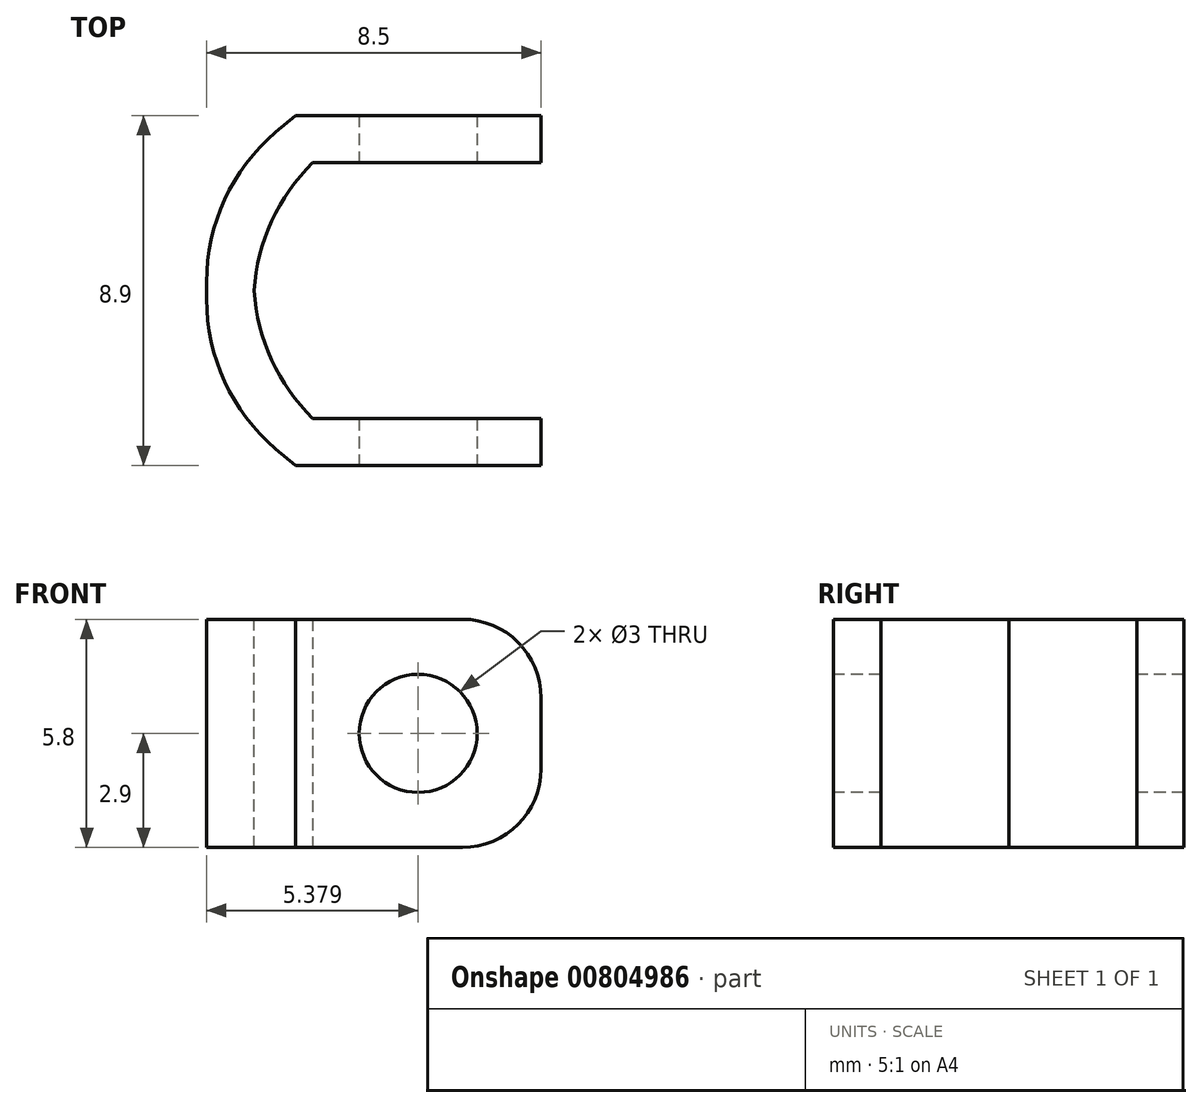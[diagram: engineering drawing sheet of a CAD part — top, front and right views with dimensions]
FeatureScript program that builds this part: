
annotation { "Feature Type Name" : "Feature", "Feature Type Description" : "" }
export const myFeature = defineFeature(function(context is Context, id is Id, definition is map)
    precondition{}
    {
        {
            assignVariable(context, id + "F0", {"name" : "nutWidth", "anyValue" : 5.8 * mm});
        }
        {
            var Q0;
            Q0=qCreatedBy(makeId("Top.planeOp"),FACE);
            var sketch = newSketch(context, id + "F1", { "sketchPlane" : qUnion([Q0])});
            skLineSegment(sketch, "E0", {"start": v(-7.3, 0) * mm, "end": v(-7.3, 1.97) * mm});
            skLineSegment(sketch, "E1", {"start": v(-7.3, 1.97) * mm, "end": v(-5.8, 3.25) * mm});
            skLineSegment(sketch, "E2", {"start": v(-5.8, 3.25) * mm, "end": v(0, 3.25) * mm});
            skLineSegment(sketch, "E3.MirrorCS", {"start": v(-7.3, 0) * mm, "end": v(-7.3, -1.97) * mm});
            skLineSegment(sketch, "E4.MirrorCS", {"start": v(-7.3, -1.97) * mm, "end": v(-5.8, -3.25) * mm});
            skLineSegment(sketch, "E5.MirrorCS", {"start": v(-5.8, -3.25) * mm, "end": v(0, -3.25) * mm});
            skLineSegment(sketch, "E6.0", {"start": v(-6.24, 4.45) * mm, "end": v(0, 4.45) * mm});
            skLineSegment(sketch, "E6.1", {"start": v(-8.5, 2.52) * mm, "end": v(-6.24, 4.45) * mm});
            skLineSegment(sketch, "E6.2", {"start": v(-6.24, -4.45) * mm, "end": v(0, -4.45) * mm});
            skLineSegment(sketch, "E6.3", {"start": v(-8.5, -2.52) * mm, "end": v(-6.24, -4.45) * mm});
            skLineSegment(sketch, "E6.4", {"start": v(-8.5, 0) * mm, "end": v(-8.5, -2.52) * mm});
            skLineSegment(sketch, "E6.5", {"start": v(-8.5, 0) * mm, "end": v(-8.5, 2.52) * mm});
            skLineSegment(sketch, "E7", {"start": v(0, 4.45) * mm, "end": v(0, 3.25) * mm});
            skLineSegment(sketch, "E8", {"start": v(0, -3.25) * mm, "end": v(0, -4.45) * mm});
            skSolve(sketch);
        }
        {
            var Q0;
            Q0 = qSketchRegion(id + "F1", true);
            extrude(context, id + "F2", {"entities" : qUnion([Q0]), "depth" : getVariable(context, 'nutWidth'), "offsetDistance" : 25 * mm});
        }
        {
            var Q0;
            Q0=makeQuery(id+"F2.opExtrude","SWEPT_EDGE",EDGE,{"disambiguationData":[OSD([sQuery(id+"F1.wireOp",EDGE,"E6.3"),sQuery(id+"F1.wireOp",EDGE,"E6.4")])]});
            var Q1;
            Q1=makeQuery(id+"F2.opExtrude","SWEPT_EDGE",EDGE,{"disambiguationData":[OSD([sQuery(id+"F1.wireOp",EDGE,"E6.1"),sQuery(id+"F1.wireOp",EDGE,"E6.5")])]});
            var Q2;
            Q2=makeQuery(id+"F2.opExtrude","SWEPT_EDGE",EDGE,{"disambiguationData":[OSD([sQuery(id+"F1.wireOp",EDGE,"E3.MirrorCS"),sQuery(id+"F1.wireOp",EDGE,"E4.MirrorCS")])]});
            var Q3;
            Q3=makeQuery(id+"F2.opExtrude","SWEPT_EDGE",EDGE,{"disambiguationData":[OSD([sQuery(id+"F1.wireOp",EDGE,"E0"),sQuery(id+"F1.wireOp",EDGE,"E1")])]});
            fillet(context, id + "F3", {"entities" : qUnion([Q0, Q1, Q2, Q3]), "radius" : 5 * mm, "tangentPropagation" : true, "allowEdgeOverflow" : false});
        }
        {
            var Q0;
            Q0=makeQuery(id+"F2.opExtrude","SWEPT_FACE",FACE,{"disambiguationData":[OSD([sQuery(id+"F1.wireOp",EDGE,"E6.2")])]});
            var sketch = newSketch(context, id + "F4", { "sketchPlane" : qUnion([Q0])});
            skLineSegment(sketch, "E9", {"start": v(-6.24, 2.9) * mm, "end": v(0, 2.9) * mm});
            skLineSegment(sketch, "E10", {"start": v(0, 2.9) * mm, "end": v(-3.12, 2.9) * mm});
            skCircle(sketch, "E11", {"center": v(-3.12, 2.9) * mm, "radius": 1.5 * mm});
            skSolve(sketch);
        }
        {
            var Q0;
            Q0 = qSketchRegion(id + "F4", true);
            extrude(context, id + "F5", {"entities" : qUnion([Q0]), "operationType" : NewBodyOperationType.REMOVE, "endBound" : BoundingType.THROUGH_ALL, "oppositeDirection" : true, "depth" : 25 * mm, "offsetDistance" : 25 * mm});
        }
        {
            var Q0;
            Q0=makeQuery(id+"F2.opExtrude","CAP_EDGE",EDGE,{"disambiguationData":[OSD([sQuery(id+"F1.wireOp",EDGE,"E7")])],"isStart":false});
            var Q1;
            Q1=makeQuery(id+"F2.opExtrude","CAP_EDGE",EDGE,{"disambiguationData":[OSD([sQuery(id+"F1.wireOp",EDGE,"E8")])],"isStart":false});
            var Q2;
            Q2=makeQuery(id+"F2.opExtrude","CAP_EDGE",EDGE,{"disambiguationData":[OSD([sQuery(id+"F1.wireOp",EDGE,"E7")])],"isStart":true});
            var Q3;
            Q3=makeQuery(id+"F2.opExtrude","CAP_EDGE",EDGE,{"disambiguationData":[OSD([sQuery(id+"F1.wireOp",EDGE,"E8")])],"isStart":true});
            fillet(context, id + "F6", {"entities" : qUnion([Q0, Q1, Q2, Q3]), "radius" : 2 * mm, "tangentPropagation" : true, "allowEdgeOverflow" : false});
        }
    });
